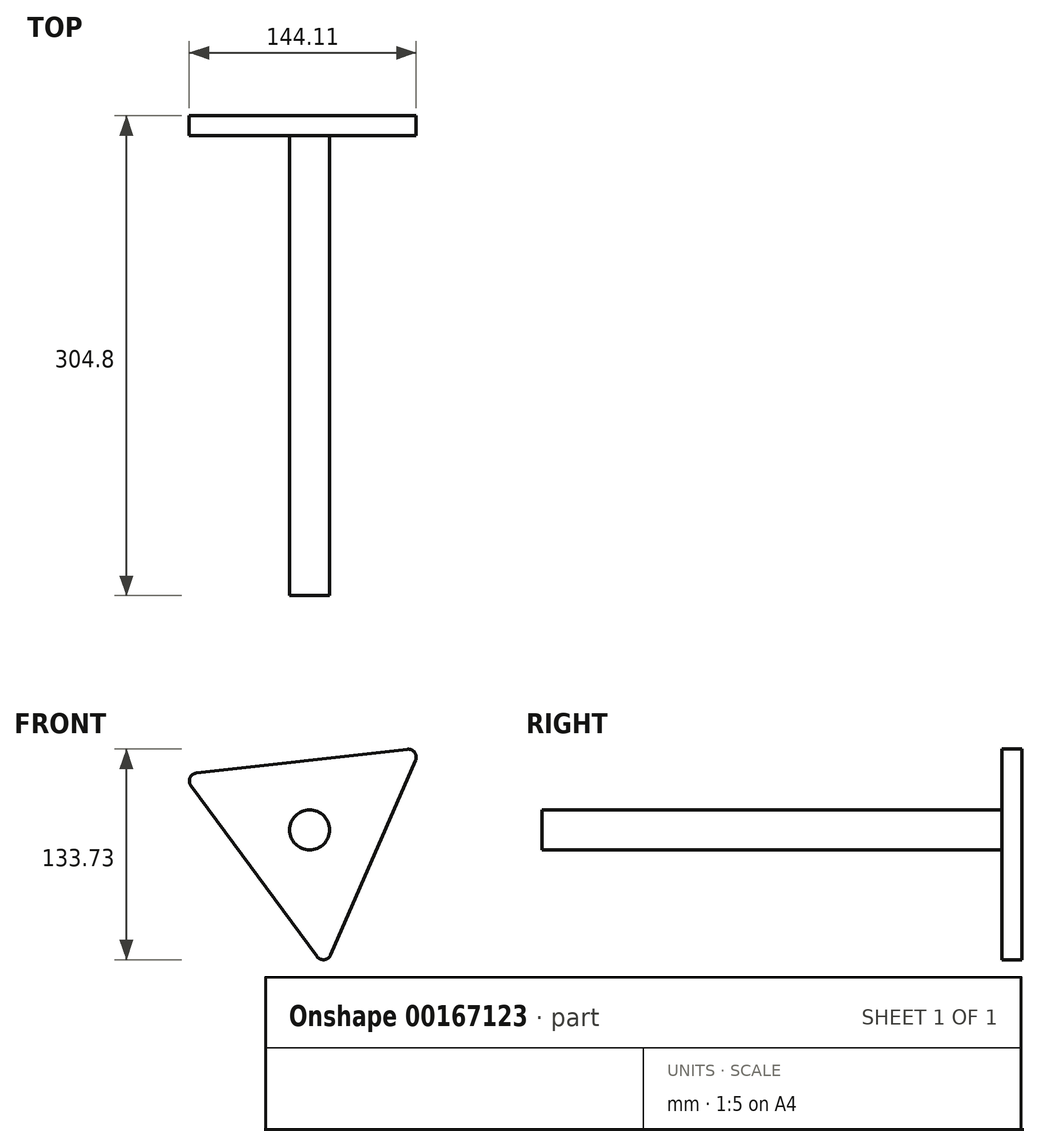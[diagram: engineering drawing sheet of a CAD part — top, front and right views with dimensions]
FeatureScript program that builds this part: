
annotation { "Feature Type Name" : "Feature", "Feature Type Description" : "" }
export const myFeature = defineFeature(function(context is Context, id is Id, definition is map)
    precondition{}
    {
        {
            var Q0;
            Q0=qCreatedBy(makeId("Front.planeOp"),FACE);
            var sketch = newSketch(context, id + "F0", { "sketchPlane" : qUnion([Q0])});
            skCircle(sketch, "E0", {"center": v(0, 0) * mm, "radius": 87.99 * mm});
            skCircle(sketch, "E1.cCircle", {"center": v(0, 0) * mm, "radius": 87.99 * mm, "construction": true});
            skLineSegment(sketch, "E1.0", {"start": v(67.27, 44.2) * mm, "end": v(13.39, -79.37) * mm});
            skLineSegment(sketch, "E1.1", {"start": v(4.64, -80.35) * mm, "end": v(-75.43, 28.1) * mm});
            skLineSegment(sketch, "E1.2", {"start": v(-71.91, 36.16) * mm, "end": v(62.04, 51.28) * mm});
            skCircle(sketch, "E2", {"center": v(0, 0) * mm, "radius": 12.7 * mm});
            skPoint(sketch, "E3.visualSharp", {"position": v(9.87, -87.43) * mm});
            skArc(sketch, "E3.filletArc", {"start": v(4.64, -80.35) * mm, "mid": v(9.3, -82.39) * mm, "end": v(13.39, -79.37) * mm});
            skPoint(sketch, "E4.visualSharp", {"position": v(-80.65, 35.17) * mm});
            skArc(sketch, "E4.filletArc", {"start": v(-71.91, 36.16) * mm, "mid": v(-76, 33.14) * mm, "end": v(-75.43, 28.1) * mm});
            skPoint(sketch, "E5.visualSharp", {"position": v(70.78, 52.26) * mm});
            skArc(sketch, "E5.filletArc", {"start": v(67.27, 44.2) * mm, "mid": v(66.7, 49.25) * mm, "end": v(62.04, 51.28) * mm});
            skSolve(sketch);
        }
        {
            var Q0;
            Q0=makeQuery(id+"F0.imprint","IMPRINT",FACE,{"disambiguationData":[TD([[makeQuery(id+"F0.imprint","IMPRINT",EDGE,{"derivedFrom":sQuery(id+"F0.wireOp",EDGE,"E1.0")}),-1.0]])]});
            extrude(context, id + "F1", {"entities" : qUnion([Q0]), "depth" : 12.7 * mm});
        }
        {
            var Q0;
            Q0=makeQuery(id+"F0.imprint","IMPRINT",FACE,{"disambiguationData":[TD([[makeQuery(id+"F0.imprint","IMPRINT",EDGE,{"derivedFrom":sQuery(id+"F0.wireOp",EDGE,"E2")}),1.0]])]});
            extrude(context, id + "F2", {"entities" : qUnion([Q0]), "operationType" : NewBodyOperationType.ADD, "depth" : 304.8 * mm});
        }
    });
